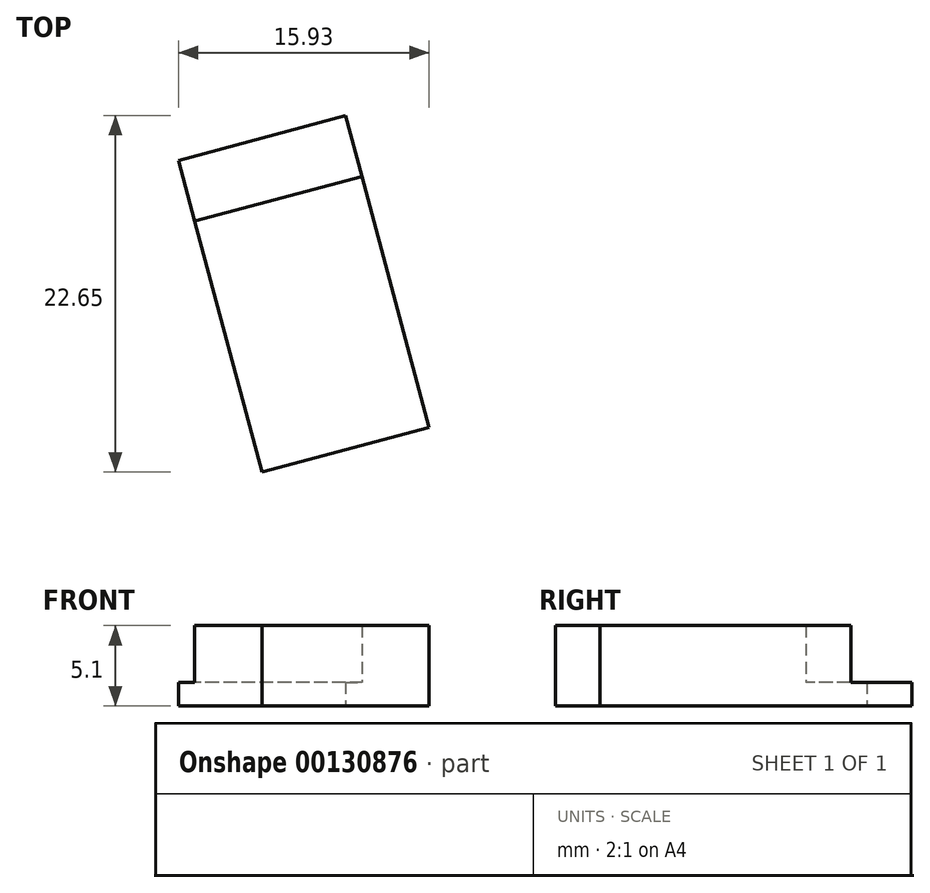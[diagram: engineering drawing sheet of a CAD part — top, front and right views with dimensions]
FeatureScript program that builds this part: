
annotation { "Feature Type Name" : "Feature", "Feature Type Description" : "" }
export const myFeature = defineFeature(function(context is Context, id is Id, definition is map)
    precondition{}
    {
        {
            var Q0;
            Q0=qCreatedBy(makeId("Top.planeOp"),FACE);
            var sketch = newSketch(context, id + "F0", { "sketchPlane" : qUnion([Q0])});
            skLineSegment(sketch, "E0.bottom", {"start": v(-5.3, 19.8) * mm, "end": v(0, 0) * mm});
            skLineSegment(sketch, "E0.top", {"start": v(-15.93, 16.95) * mm, "end": v(-10.63, -2.85) * mm});
            skLineSegment(sketch, "E0.left", {"start": v(-5.3, 19.8) * mm, "end": v(-15.93, 16.95) * mm});
            skLineSegment(sketch, "E0.right", {"start": v(0, 0) * mm, "end": v(-10.63, -2.85) * mm});
            skLineSegment(sketch, "E1", {"start": v(-4.27, 15.94) * mm, "end": v(-14.9, 13.1) * mm});
            skLineSegment(sketch, "E2", {"start": v(0.95, 0) * mm, "end": v(25.94, 0) * mm, "construction": true});
            skSolve(sketch);
        }
        {
            var Q0;
            {var subQ1=sQuery(id+"F0.wireOp",EDGE,"E0.right");Q0=makeQuery(id+"F0.imprint","IMPRINT",FACE,{"disambiguationData":[TD([[makeQuery(id+"F0.imprint","IMPRINT",EDGE,{"derivedFrom":subQ1}),-1.0]])]});}
            extrude(context, id + "F1", {"entities" : qUnion([Q0]), "depth" : 5.1 * mm});
        }
        {
            var Q0;
            {var subQ0=sQuery(id+"F0.wireOp",EDGE,"E0.left");Q0=makeQuery(id+"F0.imprint","IMPRINT",FACE,{"disambiguationData":[TD([[makeQuery(id+"F0.imprint","IMPRINT",EDGE,{"derivedFrom":subQ0}),1.0]])]});}
            extrude(context, id + "F2", {"entities" : qUnion([Q0]), "operationType" : NewBodyOperationType.ADD, "depth" : 1.5 * mm});
        }
    });
